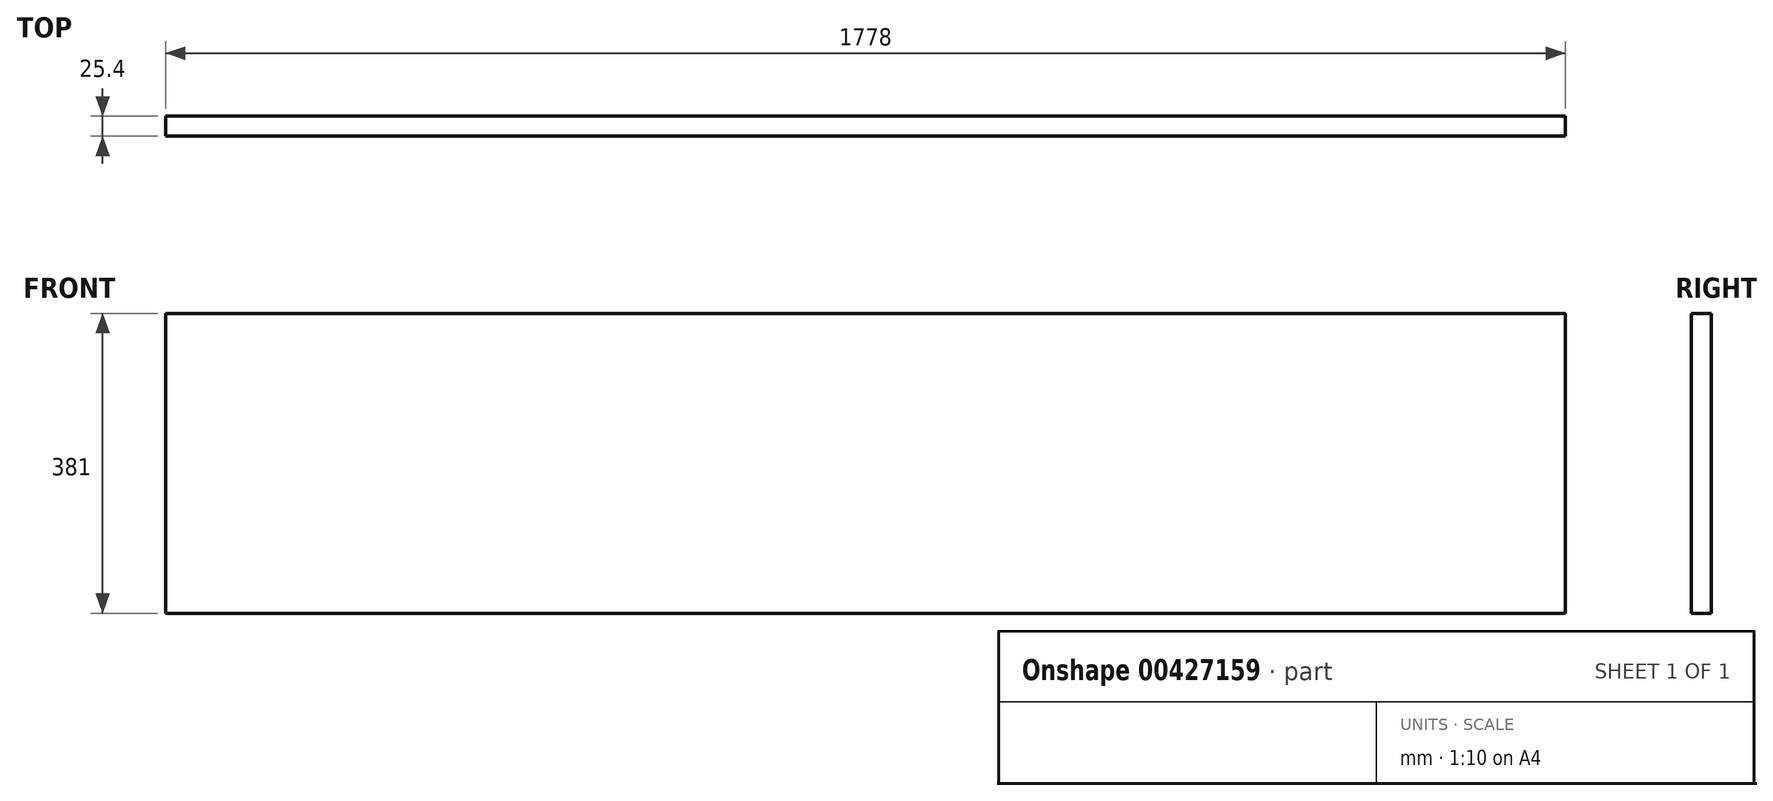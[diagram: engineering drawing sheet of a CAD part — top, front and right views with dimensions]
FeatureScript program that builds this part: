
annotation { "Feature Type Name" : "Feature", "Feature Type Description" : "" }
export const myFeature = defineFeature(function(context is Context, id is Id, definition is map)
    precondition{}
    {
        {
            var Q0;
            Q0=qCreatedBy(makeId("Front.planeOp"),FACE);
            var sketch = newSketch(context, id + "F0", { "sketchPlane" : qUnion([Q0])});
            skLineSegment(sketch, "E0.bottom", {"start": v(-20.92, 373.7) * mm, "end": v(1757.08, 373.7) * mm});
            skLineSegment(sketch, "E0.top", {"start": v(-20.92, -7.3) * mm, "end": v(1757.08, -7.3) * mm});
            skLineSegment(sketch, "E0.left", {"start": v(-20.92, 373.7) * mm, "end": v(-20.92, -7.3) * mm});
            skLineSegment(sketch, "E0.right", {"start": v(1757.08, 373.7) * mm, "end": v(1757.08, -7.3) * mm});
            skSolve(sketch);
        }
        {
            var Q0;
            Q0=makeQuery(id+"F0.imprint","IMPRINT",FACE,{"disambiguationData":[TD([[makeQuery(id+"F0.imprint","IMPRINT",EDGE,{"derivedFrom":sQuery(id+"F0.wireOp",EDGE,"E0.bottom")}),-1.0]])]});
            extrude(context, id + "F1", {"entities" : qUnion([Q0]), "depth" : 25.4 * mm});
        }
    });
